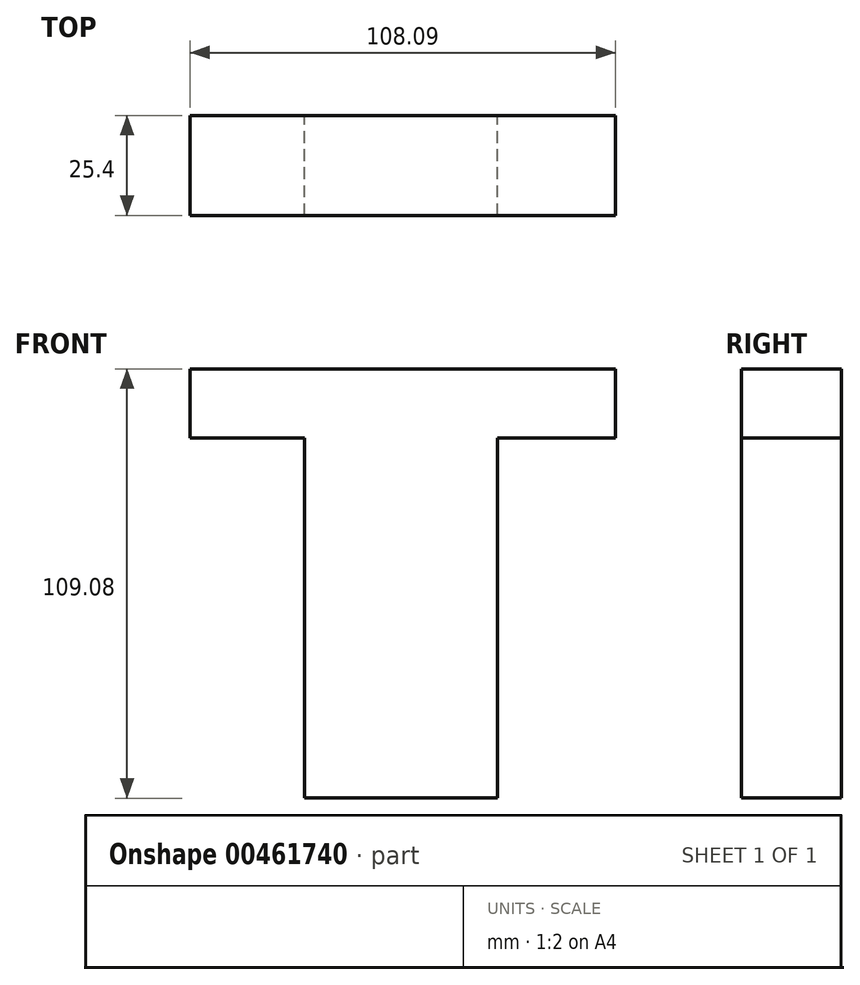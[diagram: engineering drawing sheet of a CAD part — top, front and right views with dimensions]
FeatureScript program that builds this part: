
annotation { "Feature Type Name" : "Feature", "Feature Type Description" : "" }
export const myFeature = defineFeature(function(context is Context, id is Id, definition is map)
    precondition{}
    {
        {
            var Q0;
            Q0=qCreatedBy(makeId("Front.planeOp"),FACE);
            var sketch = newSketch(context, id + "F0", { "sketchPlane" : qUnion([Q0])});
            skLineSegment(sketch, "E0", {"start": v(0, 0) * mm, "end": v(0, -35.6) * mm});
            skLineSegment(sketch, "E1", {"start": v(0, -35.6) * mm, "end": v(-24.17, -35.6) * mm});
            skLineSegment(sketch, "E2", {"start": v(-24.17, -35.6) * mm, "end": v(-24.17, 0) * mm});
            skLineSegment(sketch, "E3", {"start": v(-24.17, 0) * mm, "end": v(-24.17, 55.84) * mm});
            skLineSegment(sketch, "E4", {"start": v(-24.17, 55.84) * mm, "end": v(-53.23, 55.84) * mm});
            skLineSegment(sketch, "E5", {"start": v(-53.23, 55.84) * mm, "end": v(-53.23, 73.48) * mm});
            skLineSegment(sketch, "E6", {"start": v(-53.23, 73.48) * mm, "end": v(0, 73.48) * mm});
            skLineSegment(sketch, "E7", {"start": v(0, 73.48) * mm, "end": v(0, 0) * mm});
            skLineSegment(sketch, "E8", {"start": v(0, -35.6) * mm, "end": v(24.82, -35.6) * mm});
            skLineSegment(sketch, "E9", {"start": v(24.82, -35.6) * mm, "end": v(24.82, 0) * mm});
            skLineSegment(sketch, "E10", {"start": v(24.82, 0) * mm, "end": v(24.82, 55.84) * mm});
            skLineSegment(sketch, "E11", {"start": v(24.82, 55.84) * mm, "end": v(54.86, 55.84) * mm});
            skLineSegment(sketch, "E12", {"start": v(54.86, 55.84) * mm, "end": v(54.86, 73.48) * mm});
            skLineSegment(sketch, "E13", {"start": v(54.86, 73.48) * mm, "end": v(0, 73.48) * mm});
            skSolve(sketch);
        }
        {
            var Q0;
            Q0 = qSketchRegion(id + "F0", true);
            extrude(context, id + "F1", {"entities" : qUnion([Q0]), "depth" : 25.4 * mm, "offsetDistance" : 25.4 * mm});
        }
    });
